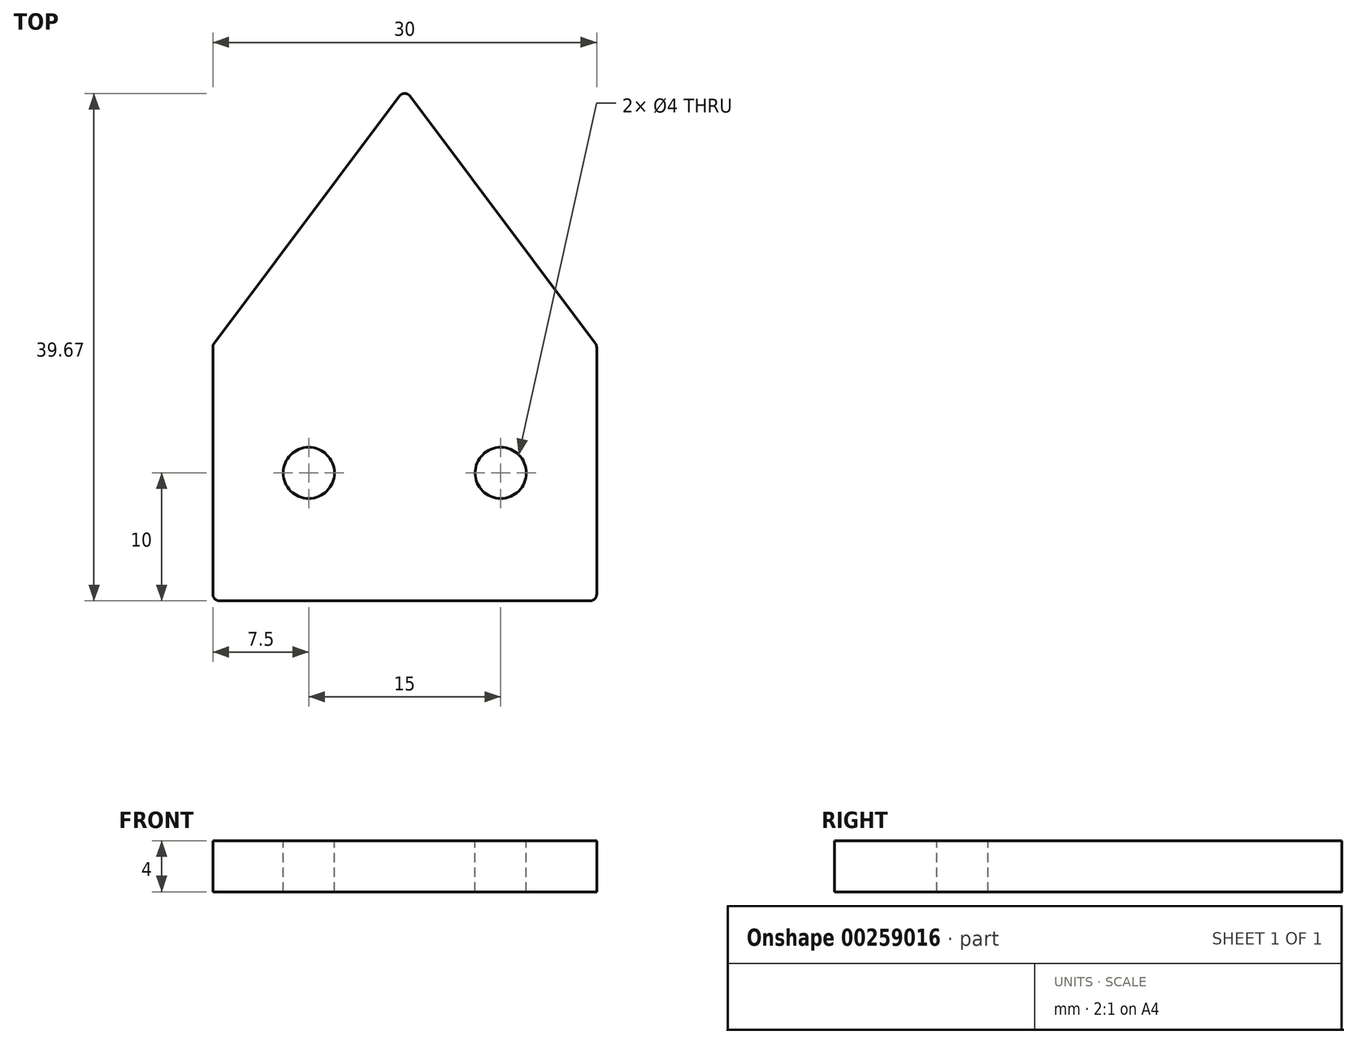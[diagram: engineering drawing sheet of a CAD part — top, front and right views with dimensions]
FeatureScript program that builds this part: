
annotation { "Feature Type Name" : "Feature", "Feature Type Description" : "" }
export const myFeature = defineFeature(function(context is Context, id is Id, definition is map)
    precondition{}
    {
        {
            var Q0;
            Q0=qCreatedBy(makeId("Top.planeOp"),FACE);
            var sketch = newSketch(context, id + "F0", { "sketchPlane" : qUnion([Q0])});
            skLineSegment(sketch, "E0.top", {"start": v(15, -10) * mm, "end": v(-15, -10) * mm});
            skLineSegment(sketch, "E0.left", {"start": v(15, 10) * mm, "end": v(15, -10) * mm});
            skLineSegment(sketch, "E0.right", {"start": v(-15, 10) * mm, "end": v(-15, -10) * mm});
            skPoint(sketch, "E0.middle", {"position": v(0, 0) * mm});
            skLineSegment(sketch, "E1", {"start": v(-15, 10) * mm, "end": v(0, 30) * mm});
            skLineSegment(sketch, "E2", {"start": v(0, 30) * mm, "end": v(15, 10) * mm});
            skLineSegment(sketch, "E3", {"start": v(0, 0) * mm, "end": v(0, 30) * mm});
            skSolve(sketch);
        }
        {
            var Q0;
            Q0=makeQuery(id+"F0.imprint","IMPRINT",FACE,{"disambiguationData":[TD([[makeQuery(id+"F0.imprint","IMPRINT",EDGE,{"derivedFrom":sQuery(id+"F0.wireOp",EDGE,"E0.top")}),-1.0]])]});
            extrude(context, id + "F1", {"entities" : qUnion([Q0]), "depth" : 4 * mm, "offsetDistance" : 25 * mm});
        }
        {
            var Q0;
            Q0=makeQuery(id+"F1.opExtrude","SWEPT_EDGE",EDGE,{"disambiguationData":[OSD([sQuery(id+"F0.wireOp",EDGE,"E0.left"),sQuery(id+"F0.wireOp",EDGE,"E2")])]});
            var Q1;
            Q1=makeQuery(id+"F1.opExtrude","SWEPT_EDGE",EDGE,{"disambiguationData":[OSD([sQuery(id+"F0.wireOp",EDGE,"E0.top"),sQuery(id+"F0.wireOp",EDGE,"E0.left")])]});
            var Q2;
            Q2=makeQuery(id+"F1.opExtrude","SWEPT_EDGE",EDGE,{"disambiguationData":[OSD([sQuery(id+"F0.wireOp",EDGE,"E1"),sQuery(id+"F0.wireOp",EDGE,"E2")])]});
            var Q3;
            Q3=makeQuery(id+"F1.opExtrude","SWEPT_EDGE",EDGE,{"disambiguationData":[OSD([sQuery(id+"F0.wireOp",EDGE,"E0.right"),sQuery(id+"F0.wireOp",EDGE,"E1")])]});
            var Q4;
            Q4=makeQuery(id+"F1.opExtrude","SWEPT_EDGE",EDGE,{"disambiguationData":[OSD([sQuery(id+"F0.wireOp",EDGE,"E0.top"),sQuery(id+"F0.wireOp",EDGE,"E0.right")])]});
            fillet(context, id + "F2", {"entities" : qUnion([Q0, Q1, Q2, Q3, Q4]), "radius" : 0.5 * mm, "tangentPropagation" : true, "allowEdgeOverflow" : false});
        }
        {
            var Q0;
            Q0=makeQuery(id+"F1.opExtrude","CAP_FACE",FACE,{"disambiguationData":[OSD([sQuery(id+"F0.wireOp",EDGE,"E0.top"),sQuery(id+"F0.wireOp",EDGE,"E0.left"),sQuery(id+"F0.wireOp",EDGE,"E0.right"),sQuery(id+"F0.wireOp",EDGE,"E1"),sQuery(id+"F0.wireOp",EDGE,"E2")])],"isStart":true});
            var sketch = newSketch(context, id + "F3", { "sketchPlane" : qUnion([Q0])});
            skLineSegment(sketch, "E4", {"start": v(0, 0) * mm, "end": v(15, 0) * mm, "construction": true});
            skLineSegment(sketch, "E5", {"start": v(0, 0) * mm, "end": v(-15, 0) * mm, "construction": true});
            skPoint(sketch, "E6", {"position": v(7.5, 0) * mm});
            skPoint(sketch, "E7", {"position": v(-7.5, 0) * mm});
            skSolve(sketch);
        }
        {
            var Q0;
            Q0=sQuery(id+"F3.wireOp",VERTEX,"E6");
            var Q1;
            Q1=sQuery(id+"F3.wireOp",VERTEX,"E7");
            var Q2;
            Q2=makeQuery(id+"F1.opExtrude","SWEPT_BODY",BODY,{"disambiguationData":[OSD([sQuery(id+"F0.wireOp",EDGE,"E0.top"),sQuery(id+"F0.wireOp",EDGE,"E0.left"),sQuery(id+"F0.wireOp",EDGE,"E0.right"),sQuery(id+"F0.wireOp",EDGE,"E1"),sQuery(id+"F0.wireOp",EDGE,"E2")])]});
            hole(context, id + "F4", {"style" : HoleStyle.SIMPLE, "endStyle" : HoleEndStyle.THROUGH, "holeDiameter" : 4 * mm, "majorDiameter" : 5 * mm, "isTappedThrough" : true, "tappedDepth" : 12 * mm, "tapClearance" : 3, "startFromSketch" : true, "locations" : qUnion([Q0, Q1]), "scope" : qUnion([Q2])});
        }
    });
